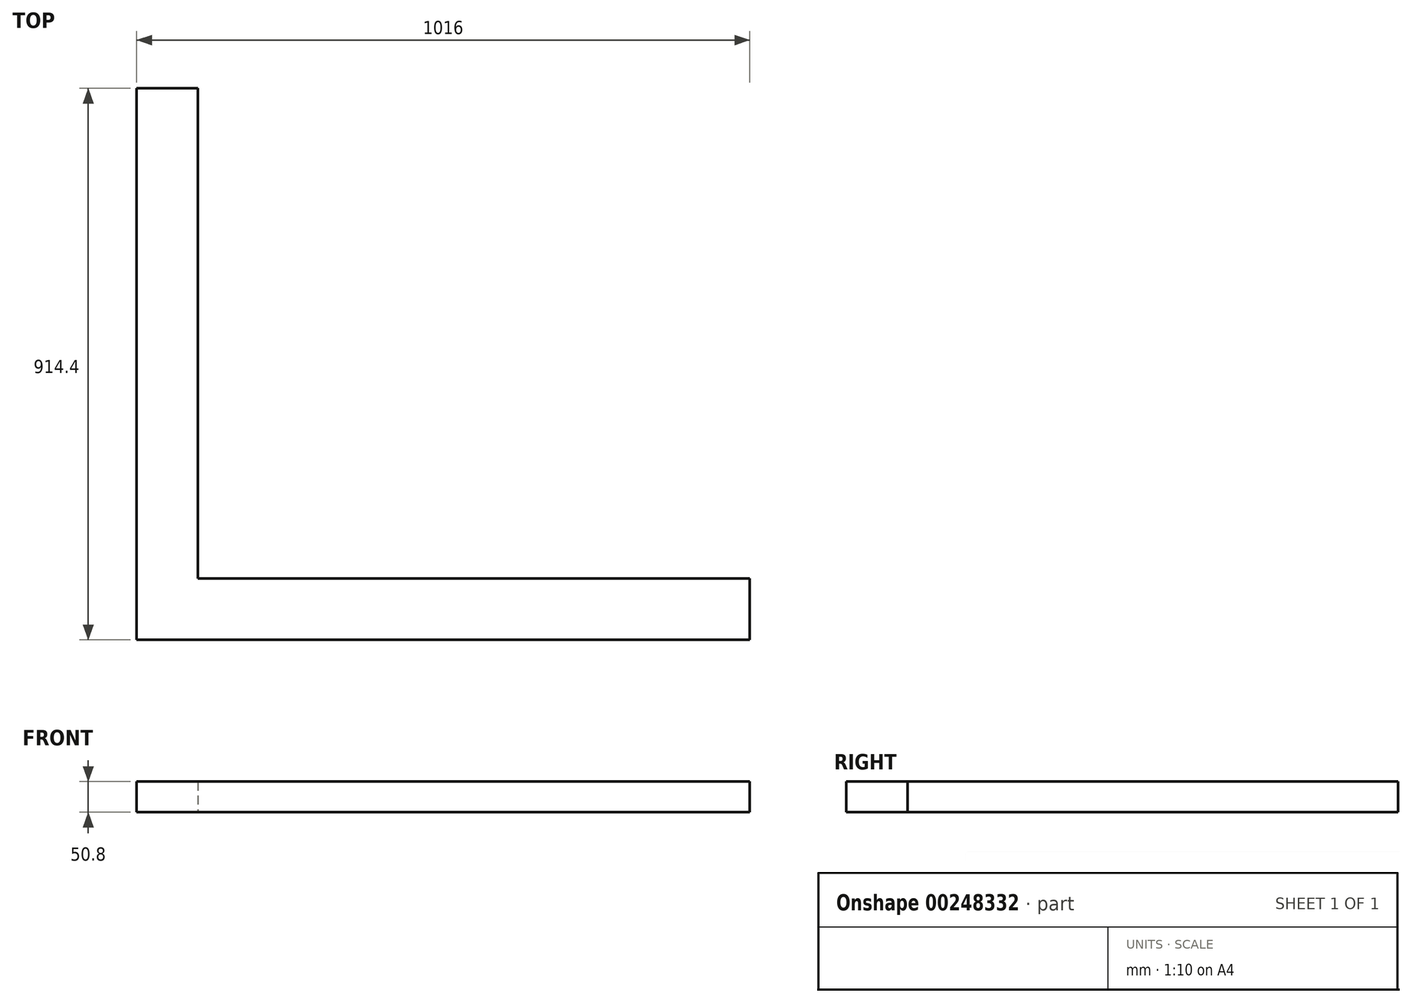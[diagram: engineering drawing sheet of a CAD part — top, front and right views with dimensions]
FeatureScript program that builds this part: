
annotation { "Feature Type Name" : "Feature", "Feature Type Description" : "" }
export const myFeature = defineFeature(function(context is Context, id is Id, definition is map)
    precondition{}
    {
        {
            var Q0;
            Q0=qCreatedBy(makeId("Front.planeOp"),FACE);
            var sketch = newSketch(context, id + "F0", { "sketchPlane" : qUnion([Q0])});
            skLineSegment(sketch, "E0.bottom", {"start": v(50.8, -25.4) * mm, "end": v(-50.8, -25.4) * mm});
            skLineSegment(sketch, "E0.top", {"start": v(50.8, 25.4) * mm, "end": v(-50.8, 25.4) * mm});
            skLineSegment(sketch, "E0.left", {"start": v(50.8, -25.4) * mm, "end": v(50.8, 25.4) * mm});
            skLineSegment(sketch, "E0.right", {"start": v(-50.8, -25.4) * mm, "end": v(-50.8, 25.4) * mm});
            skPoint(sketch, "E0.middle", {"position": v(0, 0) * mm});
            skSolve(sketch);
        }
        {
            var Q0;
            Q0 = qSketchRegion(id + "F0", true);
            extrude(context, id + "F1", {"entities" : qUnion([Q0]), "endBound" : BoundingType.SYMMETRIC, "depth" : 914.4 * mm});
        }
        {
            var Q0;
            Q0=makeQuery(id+"F1.opExtrude","SWEPT_FACE",FACE,{"disambiguationData":[OSD([sQuery(id+"F0.wireOp",EDGE,"E0.left")])]});
            var sketch = newSketch(context, id + "F2", { "sketchPlane" : qUnion([Q0])});
            skLineSegment(sketch, "E1.bottom", {"start": v(-457.2, 25.4) * mm, "end": v(-355.6, 25.4) * mm});
            skLineSegment(sketch, "E1.top", {"start": v(-457.2, -25.4) * mm, "end": v(-355.6, -25.4) * mm});
            skLineSegment(sketch, "E1.left", {"start": v(-457.2, 25.4) * mm, "end": v(-457.2, -25.4) * mm});
            skLineSegment(sketch, "E1.right", {"start": v(-355.6, 25.4) * mm, "end": v(-355.6, -25.4) * mm});
            skSolve(sketch);
        }
        {
            var Q0;
            Q0=makeQuery(id+"F2.imprint","IMPRINT",FACE,{"disambiguationData":[TD([[makeQuery(id+"F2.imprint","IMPRINT",EDGE,{"derivedFrom":sQuery(id+"F2.wireOp",EDGE,"E1.bottom")}),-1.0]])]});
            extrude(context, id + "F3", {"entities" : qUnion([Q0]), "operationType" : NewBodyOperationType.ADD, "depth" : 914.4 * mm});
        }
    });
